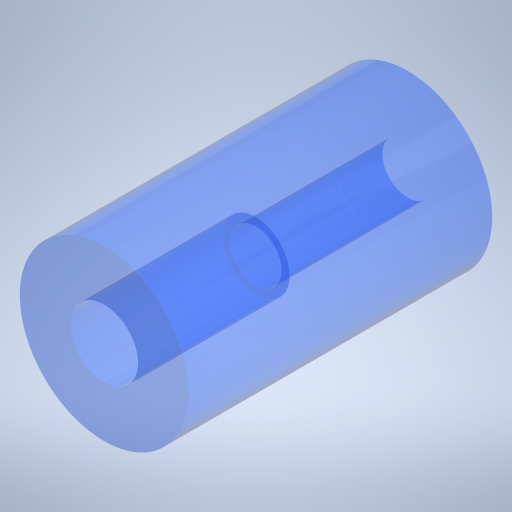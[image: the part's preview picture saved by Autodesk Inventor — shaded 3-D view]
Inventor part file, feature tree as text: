
AUTODESK INVENTOR PART (.ipt)
format: ipt  version: 2024.1 (Build 281209000, 209)  size: 272,896 bytes
history: native  units: in
note: dims shown in document units (in); Inventor stores cm internally (conversion verified against a paired STEP export)
features: extrude x2, sketch x2
ambient origin geometry x8: Origin, YZ Plane, XZ Plane, XY Plane, X Axis, Y Axis, Z Axis, Center Point
bodies: Solid1 (feature_tree)
feature tree (4):
  extrude  "Extrusion1"  Depth=0.3937in
  extrude  "Extrusion2"  Depth=0.3543in
  sketch  "Sketch1"  dims[d0=0.3937in d1=0.1181in]
  sketch  "Sketch2"  dims[d2=0.7087in d3=0.0in d4=0.1575in d5=0.3543in d6=0.0in]
